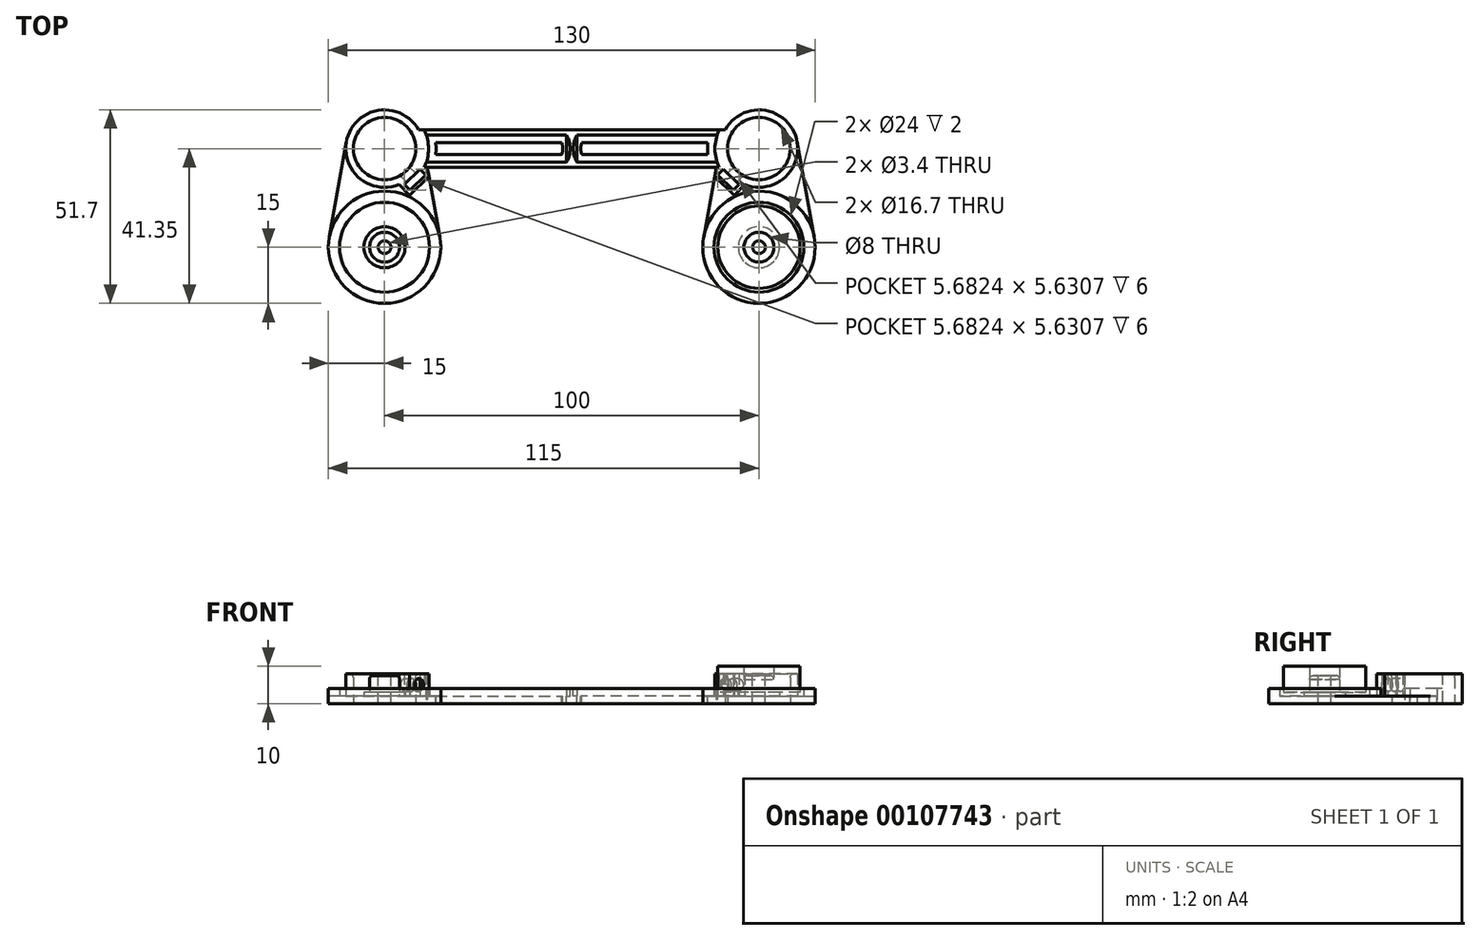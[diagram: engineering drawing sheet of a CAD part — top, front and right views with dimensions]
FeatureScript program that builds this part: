
annotation { "Feature Type Name" : "Feature", "Feature Type Description" : "" }
export const myFeature = defineFeature(function(context is Context, id is Id, definition is map)
    precondition{}
    {
        {
            assignVariable(context, id + "F0", {"name" : "BearingHeight", "anyValue" : 7});
        }
        {
            assignVariable(context, id + "F1", {"name" : "RodDistance", "anyValue" : 100});
        }
        {
            var Q0;
            Q0=qCreatedBy(makeId("Front.planeOp"),FACE);
            var sketch = newSketch(context, id + "F2", { "sketchPlane" : qUnion([Q0])});
            skLineSegment(sketch, "E0", {"start": v(0, 0) * mm, "end": v(0, 7.5) * mm});
            skLineSegment(sketch, "E1", {"start": v(0, 7.5) * mm, "end": v(4, 7.5) * mm});
            skLineSegment(sketch, "E2", {"start": v(4, 7.5) * mm, "end": v(4, 3) * mm});
            skLineSegment(sketch, "E3", {"start": v(4, 3) * mm, "end": v(5.5, 3) * mm});
            skLineSegment(sketch, "E4", {"start": v(5.5, 3) * mm, "end": v(5.5, 2) * mm});
            skLineSegment(sketch, "E5", {"start": v(5.5, 2) * mm, "end": v(11, 2) * mm});
            skLineSegment(sketch, "E6", {"start": v(11, 2) * mm, "end": v(12, 2) * mm});
            skLineSegment(sketch, "E7", {"start": v(12, 2) * mm, "end": v(12, 4) * mm});
            skLineSegment(sketch, "E8", {"start": v(12, 4) * mm, "end": v(15, 4) * mm});
            skLineSegment(sketch, "E9", {"start": v(15, 4) * mm, "end": v(15, 0) * mm});
            skLineSegment(sketch, "E10", {"start": v(15, 0) * mm, "end": v(0, 0) * mm});
            skSolve(sketch);
        }
        {
            var Q0;
            Q0=qSketchRegion(id+"F2",true);
            var Q1;
            Q1=sQuery(id+"F2.wireOp",EDGE,"E0");
            revolve(context, id + "F3", {"entities" : qUnion([Q0]), "axis" : qUnion([Q1]), "revolveType" : RevolveType.FULL});
        }
        {
            var Q0;
            Q0=makeQuery(id+"F3.opRevolve","SWEPT_FACE",FACE,{"disambiguationData":[OSD([sQuery(id+"F2.wireOp",EDGE,"E1")])]});
            var sketch = newSketch(context, id + "F4", { "sketchPlane" : qUnion([Q0])});
            skCircle(sketch, "E11", {"center": v(0, 0) * mm, "radius": 1.7 * mm});
            skSolve(sketch);
        }
        {
            var Q0;
            Q0=makeQuery(id+"F4.imprint","IMPRINT",FACE,{"disambiguationData":[TD([[makeQuery(id+"F4.imprint","IMPRINT",EDGE,{"derivedFrom":sQuery(id+"F4.wireOp",EDGE,"E11")}),1.0]])]});
            extrude(context, id + "F5", {"entities" : qUnion([Q0]), "operationType" : NewBodyOperationType.REMOVE, "endBound" : BoundingType.UP_TO_NEXT, "oppositeDirection" : true, "depth" : 25 * mm});
        }
        {
            var Q0;
            Q0=makeQuery(id+"F3.opRevolve","SWEPT_EDGE",EDGE,{"disambiguationData":[OSD([sQuery(id+"F2.wireOp",EDGE,"E1"),sQuery(id+"F2.wireOp",EDGE,"E2")])]});
            fillet(context, id + "F6", {"entities" : qUnion([Q0]), "radius" : 1 * mm, "tangentPropagation" : true, "allowEdgeOverflow" : false});
        }
        {
            var Q0;
            Q0=makeQuery(id+"F3.opRevolve","SWEPT_FACE",FACE,{"disambiguationData":[OSD([sQuery(id+"F2.wireOp",EDGE,"E10")])]});
            var sketch = newSketch(context, id + "F7", { "sketchPlane" : qUnion([Q0])});
            skCircle(sketch, "E12.0", {"center": v(0, 0) * mm, "radius": 15 * mm});
            skLineSegment(sketch, "E13", {"start": v(0, -26.35) * mm, "end": v(0, 0) * mm, "construction": true});
            skCircle(sketch, "E14", {"center": v(0, -26.35) * mm, "radius": 10.35 * mm});
            skLineSegment(sketch, "E15", {"start": v(-14.76, -2.65) * mm, "end": v(-10.19, -28.18) * mm});
            skLineSegment(sketch, "E16", {"start": v(14.76, -2.65) * mm, "end": v(10.19, -28.18) * mm});
            skCircle(sketch, "E17", {"center": v(0, -26.35) * mm, "radius": 8.35 * mm});
            skLineSegment(sketch, "E18", {"start": v(-3.82, -16.73) * mm, "end": v(-6.62, -13.88) * mm});
            skLineSegment(sketch, "E19", {"start": v(-6.62, -13.88) * mm, "end": v(-12.34, -19.47) * mm});
            skLineSegment(sketch, "E20", {"start": v(-12.34, -19.47) * mm, "end": v(-9.54, -22.33) * mm});
            skLineSegment(sketch, "E21", {"start": v(0, -26.35) * mm, "end": v(-9.48, -16.67) * mm, "construction": true});
            skLineSegment(sketch, "E22.bottom", {"start": v(-9.45, -20.85) * mm, "end": v(-5.3, -16.79) * mm});
            skLineSegment(sketch, "E22.top", {"start": v(-11, -19.28) * mm, "end": v(-6.85, -15.22) * mm});
            skLineSegment(sketch, "E22.left", {"start": v(-9.45, -20.85) * mm, "end": v(-11, -19.28) * mm});
            skLineSegment(sketch, "E22.right", {"start": v(-5.3, -16.79) * mm, "end": v(-6.85, -15.22) * mm});
            skPoint(sketch, "E22.middle", {"position": v(-8.15, -18.03) * mm});
            skLineSegment(sketch, "E23", {"start": v(-50, 9.03) * mm, "end": v(-50, -35.22) * mm, "construction": true});
            skLineSegment(sketch, "E24", {"start": v(0, -26.35) * mm, "end": v(-50, -26.35) * mm, "construction": true});
            skLineSegment(sketch, "E25", {"start": v(-9.06, -21.35) * mm, "end": v(-50, -21.35) * mm});
            skLineSegment(sketch, "E26.MirrorCS", {"start": v(-9.06, -31.35) * mm, "end": v(-50, -31.35) * mm});
            skLineSegment(sketch, "E27", {"start": v(-50, -31.35) * mm, "end": v(-50, -21.35) * mm});
            skSolve(sketch);
        }
        {
            var Q0;
            {var subQ0=sQuery(id+"F7.wireOp",EDGE,"E16");Q0=makeQuery(id+"F7.imprint","IMPRINT",FACE,{"disambiguationData":[TD([[makeQuery(id+"F7.imprint","IMPRINT",EDGE,{"derivedFrom":subQ0}),-1.0]])]});}
            var Q1;
            Q1=makeQuery(id+"F7.imprint","IMPRINT",FACE,{"disambiguationData":[TD([[makeQuery(id+"F7.imprint","IMPRINT",EDGE,{"derivedFrom":sQuery(id+"F7.wireOp",EDGE,"E17")}),-1.0]])]});
            var Q2;
            {var subQ0=sQuery(id+"F7.wireOp",EDGE,"E18");Q2=makeQuery(id+"F7.imprint","IMPRINT",FACE,{"disambiguationData":[TD([[makeQuery(id+"F7.imprint","IMPRINT",EDGE,{"derivedFrom":subQ0}),1.0]])]});}
            var Q3;
            {var subQ1=sQuery(id+"F7.wireOp",EDGE,"E22.bottom");Q3=makeQuery(id+"F7.imprint","IMPRINT",FACE,{"disambiguationData":[TD([[makeQuery(id+"F7.imprint","IMPRINT",EDGE,{"derivedFrom":subQ1}),1.0]])]});}
            var Q4;
            {var subQ0=sQuery(id+"F7.wireOp",EDGE,"E15");var subQ1=sQuery(id+"F7.wireOp",EDGE,"E14");var subQ2=makeQuery(id+"F7.imprint","INTERSECT",VERTEX,{"derivedFrom":[subQ1,subQ0]});Q4=makeQuery(id+"F7.imprint","IMPRINT",FACE,{"disambiguationData":[TD([[makeQuery(id+"F7.imprint","IMPRINT",EDGE,{"disambiguationData":[TD([[subQ2,1.0]])],"derivedFrom":subQ1}),-1.0]])]});}
            var Q5;
            Q5=makeQuery(id+"F7.imprint","IMPRINT",FACE,{"disambiguationData":[TD([[makeQuery(id+"F7.imprint","IMPRINT",EDGE,{"derivedFrom":makeQuery(id+"F5.boolean.opBoolean","COPY",EDGE,{"derivedFrom":makeQuery(id+"F5.opExtrude","TWEAK_EDGE",EDGE,{"derivedFrom":[makeQuery(id+"F3.opRevolve","SWEPT_FACE",FACE,{"disambiguationData":[OSD([sQuery(id+"F2.wireOp",EDGE,"E10")])]}),makeQuery(id+"F4.imprint","IMPRINT",EDGE,{"derivedFrom":sQuery(id+"F4.wireOp",EDGE,"E11")})]})})}),-1.0]])]});
            var Q6;
            Q6=makeQuery(id+"F3.opRevolve","SWEPT_FACE",FACE,{"disambiguationData":[OSD([sQuery(id+"F2.wireOp",EDGE,"E10")])]});
            var Q7;
            Q7=makeQuery(id+"F7.imprint","IMPRINT",FACE,{"disambiguationData":[TD([[makeQuery(id+"F7.imprint","IMPRINT",EDGE,{"derivedFrom":sQuery(id+"F7.wireOp",EDGE,"bac2def9-7b5b-4e3d-a74a-6b2987ab829d0.MirrorCS")}),1.0]])]});
            var Q8;
            Q8=makeQuery(id+"F7.imprint","IMPRINT",FACE,{"disambiguationData":[TD([[makeQuery(id+"F7.imprint","IMPRINT",EDGE,{"derivedFrom":sQuery(id+"F7.wireOp",EDGE,"bac2def9-7b5b-4e3d-a74a-6b2987ab829d0.MirrorCS")}),-1.0]])]});
            var Q9;
            {var subQ10=sQuery(id+"F7.wireOp",EDGE,"E18");Q9=makeQuery(id+"F7.imprint","IMPRINT",FACE,{"disambiguationData":[TD([[makeQuery(id+"F7.imprint","IMPRINT",EDGE,{"derivedFrom":subQ10}),-1.0]])]});}
            var Q10;
            {var subQ0=sQuery(id+"F7.wireOp",EDGE,"E26.MirrorCS");Q10=makeQuery(id+"F7.imprint","IMPRINT",FACE,{"disambiguationData":[TD([[makeQuery(id+"F7.imprint","IMPRINT",EDGE,{"derivedFrom":subQ0}),-1.0]])]});}
            var Q11;
            {var subQ0=sQuery(id+"F7.wireOp",EDGE,"E20");var subQ1=sQuery(id+"F7.wireOp",EDGE,"E14");var subQ2=makeQuery(id+"F7.imprint","INTERSECT",VERTEX,{"derivedFrom":[subQ1,subQ0]});Q11=makeQuery(id+"F7.imprint","IMPRINT",FACE,{"disambiguationData":[TD([[makeQuery(id+"F7.imprint","IMPRINT",EDGE,{"disambiguationData":[TD([[subQ2,1.0]])],"derivedFrom":subQ1}),-1.0]])]});}
            var Q12;
            Q12=makeQuery(id+"F7.imprint","IMPRINT",FACE,{"disambiguationData":[TD([[makeQuery(id+"F7.imprint","IMPRINT",EDGE,{"derivedFrom":sQuery(id+"F7.wireOp",EDGE,"5ed84967-02fd-4a5b-a8fa-f03f07f36d90")}),1.0]])]});
            var Q13;
            Q13=makeQuery(id+"F3.opRevolve","SWEPT_FACE",FACE,{"disambiguationData":[OSD([sQuery(id+"F2.wireOp",EDGE,"E5"),sQuery(id+"F2.wireOp",EDGE,"E6")])]});
            extrude(context, id + "F8", {"entities" : qUnion([Q0, Q1, Q2, Q3, Q4, Q5, Q6, Q7, Q8, Q9, Q10, Q11, Q12]), "operationType" : NewBodyOperationType.ADD, "endBound" : BoundingType.UP_TO_SURFACE, "oppositeDirection" : true, "endBoundEntityFace" : qUnion([Q13]), "depth" : 25 * mm});
        }
        {
            var Q0;
            Q0=makeQuery(id+"F7.imprint","IMPRINT",FACE,{"disambiguationData":[TD([[makeQuery(id+"F7.imprint","IMPRINT",EDGE,{"derivedFrom":sQuery(id+"F7.wireOp",EDGE,"E17")}),-1.0]])]});
            var Q1;
            {var subQ0=sQuery(id+"F7.wireOp",EDGE,"E18");Q1=makeQuery(id+"F7.imprint","IMPRINT",FACE,{"disambiguationData":[TD([[makeQuery(id+"F7.imprint","IMPRINT",EDGE,{"derivedFrom":subQ0}),1.0]])]});}
            var Q2;
            Q2=makeQuery(id+"F7.imprint","IMPRINT",FACE,{"disambiguationData":[TD([[makeQuery(id+"F7.imprint","IMPRINT",EDGE,{"derivedFrom":sQuery(id+"F7.wireOp",EDGE,"bac2def9-7b5b-4e3d-a74a-6b2987ab829d0.MirrorCS")}),1.0]])]});
            extrude(context, id + "F9", {"entities" : qUnion([Q0, Q1, Q2]), "operationType" : NewBodyOperationType.ADD, "oppositeDirection" : true, "depth" : 8 * mm});
        }
        {
            var Q0;
            Q0=makeQuery(id+"F9.opExtrude","SWEPT_FACE",FACE,{"disambiguationData":[OSD([sQuery(id+"F7.wireOp",EDGE,"E19")])]});
            var sketch = newSketch(context, id + "F10", { "sketchPlane" : qUnion([Q0])});
            skLineSegment(sketch, "E28", {"start": v(-14.44, 5) * mm, "end": v(-21.74, 5) * mm, "construction": true});
            skPoint(sketch, "E29", {"position": v(-18.1, 5) * mm});
            skCircle(sketch, "E30", {"center": v(-18.1, 5) * mm, "radius": 1.7 * mm});
            skSolve(sketch);
        }
        {
            var Q0;
            Q0=makeQuery(id+"F10.imprint","IMPRINT",FACE,{"disambiguationData":[TD([[makeQuery(id+"F10.imprint","IMPRINT",EDGE,{"derivedFrom":sQuery(id+"F10.wireOp",EDGE,"E30")}),1.0]])]});
            var Q1;
            {var subQ0=sQuery(id+"F7.wireOp",EDGE,"E17");Q1=makeQuery(id+"F9.boolean.opBoolean","MERGE",FACE,{"derivedFrom":[makeQuery(id+"F8.opExtrude","SWEPT_FACE",FACE,{"disambiguationData":[OSD([subQ0])]}),makeQuery(id+"F9.opExtrude","SWEPT_FACE",FACE,{"disambiguationData":[OSD([subQ0])]})]});}
            extrude(context, id + "F11", {"entities" : qUnion([Q0]), "operationType" : NewBodyOperationType.REMOVE, "endBound" : BoundingType.UP_TO_SURFACE, "oppositeDirection" : true, "endBoundEntityFace" : qUnion([Q1]), "depth" : 25 * mm});
        }
        {
            var Q0;
            Q0=makeQuery(id+"F3.opRevolve","SWEPT_FACE",FACE,{"disambiguationData":[OSD([sQuery(id+"F2.wireOp",EDGE,"E3")])]});
            var sketch = newSketch(context, id + "F12", { "sketchPlane" : qUnion([Q0])});
            skCircle(sketch, "E31.0", {"center": v(0, 0) * mm, "radius": 4 * mm});
            skCircle(sketch, "E32", {"center": v(0, 0) * mm, "radius": 11 * mm});
            skSolve(sketch);
        }
        {
            var Q0;
            Q0=qSketchRegion(id+"F12",true);
            extrude(context, id + "F13", {"entities" : qUnion([Q0]), "depth" : (getVariable(context, 'BearingHeight')) * mm});
        }
        {
            var Q0;
            Q0=makeQuery(id+"F9.opExtrude","CAP_EDGE",EDGE,{"disambiguationData":[OSD([sQuery(id+"F7.wireOp",EDGE,"E17")])],"isStart":false});
            fillet(context, id + "F14", {"entities" : qUnion([Q0]), "radius" : 1 * mm, "tangentPropagation" : true, "allowEdgeOverflow" : false});
        }
        {
            var Q0;
            {var subQ0=sQuery(id+"F7.wireOp",EDGE,"E26.MirrorCS");var subQ1=sQuery(id+"F7.wireOp",EDGE,"E25");var subQ2=sQuery(id+"F7.wireOp",EDGE,"E20");var subQ3=sQuery(id+"F7.wireOp",EDGE,"E16");var subQ4=sQuery(id+"F7.wireOp",EDGE,"E14");var subQ7=sQuery(id+"F7.wireOp",EDGE,"E15");var subQ10=sQuery(id+"F7.wireOp",EDGE,"E27");var subQ11=sQuery(id+"F2.wireOp",EDGE,"E10");Q0=makeQuery(id+"F9.boolean.opBoolean","SPLIT",FACE,{"disambiguationData":[TD([makeQuery(id+"F8.opExtrude","SWEPT_FACE",FACE,{"disambiguationData":[OSD([subQ2])]})])],"derivedFrom":makeQuery(id+"F8.boolean.opBoolean","MERGE",FACE,{"derivedFrom":[makeQuery(id+"F8.opExtrude","CAP_FACE",FACE,{"disambiguationData":[OSD([subQ11])],"isStart":false}),makeQuery(id+"F8.opExtrude","CAP_FACE",FACE,{"disambiguationData":[OSD([subQ11,sQuery(id+"F4.wireOp",EDGE,"E11"),sQuery(id+"F7.wireOp",EDGE,"E12.0"),subQ4,subQ7,subQ3,sQuery(id+"F7.wireOp",EDGE,"E17"),subQ2,subQ1,subQ0,subQ10])],"isStart":false})]})});}
            var sketch = newSketch(context, id + "F15", { "sketchPlane" : qUnion([Q0])});
            skLineSegment(sketch, "E33.0", {"start": v(-48.6, 22.75) * mm, "end": v(-11.18, 22.75) * mm});
            skLineSegment(sketch, "E33.1", {"start": v(-48.6, 22.75) * mm, "end": v(-48.6, 29.95) * mm});
            skLineSegment(sketch, "E33.2", {"start": v(-48.6, 29.95) * mm, "end": v(-11.18, 29.95) * mm});
            skArc(sketch, "E33.3", {"start": v(-11.18, 22.75) * mm, "mid": v(-11.75, 26.35) * mm, "end": v(-11.18, 29.95) * mm});
            skSolve(sketch);
        }
        {
            var Q0;
            Q0=makeQuery(id+"F15.imprint","IMPRINT",FACE,{"disambiguationData":[TD([[makeQuery(id+"F15.imprint","IMPRINT",EDGE,{"derivedFrom":sQuery(id+"F15.wireOp",EDGE,"E33.0")}),-1.0]])]});
            extrude(context, id + "F16", {"entities" : qUnion([Q0]), "operationType" : NewBodyOperationType.ADD, "depth" : 2 * mm});
        }
        {
            var Q0;
            {var subQ0=makeQuery(id+"F16.opExtrude","CAP_FACE",FACE,{"disambiguationData":[OSD([sQuery(id+"F2.wireOp",EDGE,"E10"),sQuery(id+"F4.wireOp",EDGE,"E11"),sQuery(id+"F7.wireOp",EDGE,"E12.0"),sQuery(id+"F7.wireOp",EDGE,"E14"),sQuery(id+"F7.wireOp",EDGE,"E15"),sQuery(id+"F7.wireOp",EDGE,"E16"),sQuery(id+"F7.wireOp",EDGE,"E17"),sQuery(id+"F7.wireOp",EDGE,"E20"),sQuery(id+"F7.wireOp",EDGE,"E25"),sQuery(id+"F7.wireOp",EDGE,"E26.MirrorCS"),sQuery(id+"F7.wireOp",EDGE,"E27"),sQuery(id+"F15.wireOp",EDGE,"E33.0"),sQuery(id+"F15.wireOp",EDGE,"E33.1"),sQuery(id+"F15.wireOp",EDGE,"E33.2"),sQuery(id+"F15.wireOp",EDGE,"E33.3")])],"isStart":false});Q0=makeQuery(id+"F25.boolean.opBoolean","MERGE",FACE,{"derivedFrom":[subQ0,makeQuery(id+"F25.opPattern","COPY",FACE,{"derivedFrom":subQ0,"instanceName":"1"})]});}
            var sketch = newSketch(context, id + "F17", { "sketchPlane" : qUnion([Q0])});
            skArc(sketch, "E34.0", {"start": v(-10.29, 20.67) * mm, "mid": v(-11.75, 26.35) * mm, "end": v(-10.29, 32.03) * mm});
            skLineSegment(sketch, "E35", {"start": v(-9.06, 31.35) * mm, "end": v(-10.63, 31.35) * mm});
            skLineSegment(sketch, "E36", {"start": v(-9.06, 21.35) * mm, "end": v(-10.63, 21.35) * mm});
            skArc(sketch, "E37", {"start": v(-48.6, 29.95) * mm, "mid": v(-49.6, 26.35) * mm, "end": v(-48.6, 22.75) * mm});
            skSolve(sketch);
        }
        {
            var Q0;
            Q0=qSketchRegion(id+"F17",true);
            var Q1;
            Q1=makeQuery(id+"F17.imprint","IMPRINT",FACE,{"disambiguationData":[TD([[makeQuery(id+"F17.imprint","IMPRINT",EDGE,{"derivedFrom":sQuery(id+"F17.wireOp",EDGE,"E37")}),1.0]])]});
            var Q2;
            {var subQ0=sQuery(id+"F7.wireOp",EDGE,"E26.MirrorCS");var subQ1=sQuery(id+"F7.wireOp",EDGE,"E25");var subQ2=sQuery(id+"F7.wireOp",EDGE,"E20");var subQ3=sQuery(id+"F7.wireOp",EDGE,"E16");var subQ4=sQuery(id+"F7.wireOp",EDGE,"E14");var subQ7=sQuery(id+"F7.wireOp",EDGE,"E15");var subQ10=sQuery(id+"F7.wireOp",EDGE,"E27");var subQ11=sQuery(id+"F2.wireOp",EDGE,"E10");Q2=makeQuery(id+"F9.boolean.opBoolean","SPLIT",FACE,{"disambiguationData":[TD([makeQuery(id+"F8.opExtrude","SWEPT_FACE",FACE,{"disambiguationData":[OSD([subQ2])]})])],"derivedFrom":makeQuery(id+"F8.boolean.opBoolean","MERGE",FACE,{"derivedFrom":[makeQuery(id+"F8.opExtrude","CAP_FACE",FACE,{"disambiguationData":[OSD([subQ11])],"isStart":false}),makeQuery(id+"F8.opExtrude","CAP_FACE",FACE,{"disambiguationData":[OSD([subQ11,sQuery(id+"F4.wireOp",EDGE,"E11"),sQuery(id+"F7.wireOp",EDGE,"E12.0"),subQ4,subQ7,subQ3,sQuery(id+"F7.wireOp",EDGE,"E17"),subQ2,subQ1,subQ0,subQ10])],"isStart":false})]})});}
            extrude(context, id + "F18", {"entities" : qUnion([Q0, Q1]), "operationType" : NewBodyOperationType.REMOVE, "endBound" : BoundingType.UP_TO_SURFACE, "oppositeDirection" : true, "endBoundEntityFace" : qUnion([Q2]), "depth" : 25 * mm});
        }
        {
            var Q0;
            {var subQ1=makeQuery(id+"F16.opExtrude","CAP_EDGE",EDGE,{"disambiguationData":[OSD([sQuery(id+"F15.wireOp",EDGE,"E33.0")])],"isStart":false});Q0=makeQuery(id+"F17.imprint","IMPRINT",FACE,{"disambiguationData":[TD([[makeQuery(id+"F17.imprint","IMPRINT",EDGE,{"derivedFrom":subQ1}),1.0]])]});}
            var sketch = newSketch(context, id + "F19", { "sketchPlane" : qUnion([Q0])});
            skArc(sketch, "E38.0", {"start": v(-13.66, 24.75) * mm, "mid": v(-13.75, 26.35) * mm, "end": v(-13.66, 27.95) * mm});
            skLineSegment(sketch, "E38.1", {"start": v(-47.34, 24.75) * mm, "end": v(-13.66, 24.75) * mm});
            skArc(sketch, "E38.2", {"start": v(-47.34, 27.95) * mm, "mid": v(-47.6, 26.35) * mm, "end": v(-47.34, 24.75) * mm});
            skLineSegment(sketch, "E38.3", {"start": v(-47.34, 27.95) * mm, "end": v(-13.66, 27.95) * mm});
            skSolve(sketch);
        }
        {
            var Q0;
            Q0=makeQuery(id+"F19.imprint","IMPRINT",FACE,{"disambiguationData":[TD([[makeQuery(id+"F19.imprint","IMPRINT",EDGE,{"derivedFrom":sQuery(id+"F19.wireOp",EDGE,"E38.0")}),1.0]])]});
            extrude(context, id + "F20", {"entities" : qUnion([Q0]), "operationType" : NewBodyOperationType.REMOVE, "oppositeDirection" : true, "depth" : 25 * mm});
        }
        {
            var Q0;
            {var subQ0=sQuery(id+"F7.wireOp",EDGE,"E20");var subQ1=sQuery(id+"F7.wireOp",EDGE,"E15");var subQ2=makeQuery(id+"F7.imprint","INTERSECT",VERTEX,{"derivedFrom":[subQ1,subQ0]});Q0=makeQuery(id+"F7.imprint","IMPRINT",FACE,{"disambiguationData":[TD([[makeQuery(id+"F7.imprint","IMPRINT",EDGE,{"disambiguationData":[TD([[subQ2,-1.0]])],"derivedFrom":subQ1}),1.0]])]});}
            var Q1;
            {var subQ0=makeQuery(id+"F16.opExtrude","CAP_FACE",FACE,{"disambiguationData":[OSD([sQuery(id+"F2.wireOp",EDGE,"E10"),sQuery(id+"F4.wireOp",EDGE,"E11"),sQuery(id+"F7.wireOp",EDGE,"E12.0"),sQuery(id+"F7.wireOp",EDGE,"E14"),sQuery(id+"F7.wireOp",EDGE,"E15"),sQuery(id+"F7.wireOp",EDGE,"E16"),sQuery(id+"F7.wireOp",EDGE,"E17"),sQuery(id+"F7.wireOp",EDGE,"E20"),sQuery(id+"F7.wireOp",EDGE,"E25"),sQuery(id+"F7.wireOp",EDGE,"E26.MirrorCS"),sQuery(id+"F7.wireOp",EDGE,"E27"),sQuery(id+"F15.wireOp",EDGE,"E33.0"),sQuery(id+"F15.wireOp",EDGE,"E33.1"),sQuery(id+"F15.wireOp",EDGE,"E33.2"),sQuery(id+"F15.wireOp",EDGE,"E33.3")])],"isStart":false});Q1=makeQuery(id+"F25.boolean.opBoolean","MERGE",FACE,{"derivedFrom":[subQ0,makeQuery(id+"F25.opPattern","COPY",FACE,{"derivedFrom":subQ0,"instanceName":"1"})]});}
            extrude(context, id + "F21", {"entities" : qUnion([Q0]), "operationType" : NewBodyOperationType.ADD, "endBound" : BoundingType.UP_TO_SURFACE, "oppositeDirection" : true, "endBoundEntityFace" : qUnion([Q1]), "depth" : 25 * mm});
        }
        {
            var Q0;
            {var subQ0=sQuery(id+"F17.wireOp",EDGE,"E35");Q0=makeQuery(id+"F17.imprint","IMPRINT",FACE,{"disambiguationData":[TD([[makeQuery(id+"F17.imprint","IMPRINT",EDGE,{"derivedFrom":subQ0}),-1.0]])]});}
            var sketch = newSketch(context, id + "F22", { "sketchPlane" : qUnion([Q0])});
            skArc(sketch, "E39.0.0", {"start": v(-11.18, 22.75) * mm, "mid": v(-10.93, 22.04) * mm, "end": v(-10.63, 21.35) * mm});
            skLineSegment(sketch, "E39.0.1", {"start": v(-10.63, 21.35) * mm, "end": v(-10.5, 21.35) * mm});
            skLineSegment(sketch, "E39.0.2", {"start": v(-10.5, 21.35) * mm, "end": v(-9.06, 21.35) * mm});
            skArc(sketch, "E39.0.3", {"start": v(-9.06, 21.35) * mm, "mid": v(-10.35, 26.35) * mm, "end": v(-9.06, 31.35) * mm});
            skLineSegment(sketch, "E39.0.4", {"start": v(-9.06, 31.35) * mm, "end": v(-10.63, 31.35) * mm});
            skArc(sketch, "E39.0.5", {"start": v(-10.63, 31.35) * mm, "mid": v(-10.93, 30.66) * mm, "end": v(-11.18, 29.95) * mm});
            skArc(sketch, "E39.0.6", {"start": v(-11.18, 29.95) * mm, "mid": v(-11.75, 26.35) * mm, "end": v(-11.18, 22.75) * mm});
            skLineSegment(sketch, "E39.1", {"start": v(-9.06, 21.35) * mm, "end": v(-50, 21.35) * mm});
            skLineSegment(sketch, "E39.2", {"start": v(-14.76, 2.65) * mm, "end": v(-10.19, 28.18) * mm});
            skLineSegment(sketch, "E39.3", {"start": v(-12.34, 19.47) * mm, "end": v(-9.54, 22.33) * mm});
            skSolve(sketch);
        }
        {
            var Q0;
            {var subQ3=sQuery(id+"F22.wireOp",EDGE,"E39.0.0");var subQ7=sQuery(id+"F22.wireOp",EDGE,"E39.1");var subQ9=makeQuery(id+"F22.imprint","INTERSECT",VERTEX,{"derivedFrom":[subQ3,subQ7]});Q0=makeQuery(id+"F22.imprint","IMPRINT",FACE,{"disambiguationData":[TD([[makeQuery(id+"F22.imprint","IMPRINT",EDGE,{"disambiguationData":[TD([[subQ9,-1.0]])],"derivedFrom":subQ3}),-1.0]])]});}
            var Q1;
            {var subQ0=sQuery(id+"F22.wireOp",EDGE,"E39.1");var subQ1=sQuery(id+"F22.wireOp",EDGE,"E39.0.0");var subQ2=makeQuery(id+"F22.imprint","INTERSECT",VERTEX,{"derivedFrom":[subQ1,subQ0]});Q1=makeQuery(id+"F22.imprint","IMPRINT",FACE,{"disambiguationData":[TD([[makeQuery(id+"F22.imprint","IMPRINT",EDGE,{"disambiguationData":[TD([[subQ2,-1.0]])],"derivedFrom":subQ1}),1.0]])]});}
            var Q2;
            {var subQ0=sQuery(id+"F22.wireOp",EDGE,"E39.1");var subQ1=makeQuery(id+"F22.imprint","INTERSECT",VERTEX,{"derivedFrom":[sQuery(id+"F22.wireOp",EDGE,"E39.0.0"),subQ0]});Q2=makeQuery(id+"F22.imprint","IMPRINT",FACE,{"disambiguationData":[TD([[makeQuery(id+"F22.imprint","IMPRINT",EDGE,{"disambiguationData":[TD([[subQ1,-1.0]])],"derivedFrom":subQ0}),1.0]])]});}
            var Q3;
            {var subQ0=sQuery(id+"F22.wireOp",EDGE,"E39.1");var subQ1=sQuery(id+"F22.wireOp",EDGE,"E39.0.3");var subQ2=makeQuery(id+"F22.imprint","INTERSECT",VERTEX,{"derivedFrom":[subQ1,subQ0]});Q3=makeQuery(id+"F22.imprint","IMPRINT",FACE,{"disambiguationData":[TD([[makeQuery(id+"F22.imprint","IMPRINT",EDGE,{"disambiguationData":[TD([[subQ2,-1.0]])],"derivedFrom":subQ1}),1.0]])]});}
            var Q4;
            {var subQ0=sQuery(id+"F17.wireOp",EDGE,"E35");Q4=makeQuery(id+"F17.imprint","IMPRINT",FACE,{"disambiguationData":[TD([[makeQuery(id+"F17.imprint","IMPRINT",EDGE,{"derivedFrom":subQ0}),-1.0]])]});}
            var Q5;
            Q5=makeQuery(id+"F9.opExtrude","CAP_FACE",FACE,{"disambiguationData":[OSD([sQuery(id+"F7.wireOp",EDGE,"E14"),sQuery(id+"F7.wireOp",EDGE,"E15"),sQuery(id+"F7.wireOp",EDGE,"E17"),sQuery(id+"F7.wireOp",EDGE,"E18"),sQuery(id+"F7.wireOp",EDGE,"E19"),sQuery(id+"F7.wireOp",EDGE,"E20"),sQuery(id+"F7.wireOp",EDGE,"E22.bottom"),sQuery(id+"F7.wireOp",EDGE,"E22.top"),sQuery(id+"F7.wireOp",EDGE,"E22.left"),sQuery(id+"F7.wireOp",EDGE,"E22.right"),sQuery(id+"F7.wireOp",EDGE,"E25")])],"isStart":false});
            extrude(context, id + "F23", {"entities" : qUnion([Q0, Q1, Q2, Q3, Q4]), "operationType" : NewBodyOperationType.ADD, "endBound" : BoundingType.UP_TO_SURFACE, "endBoundEntityFace" : qUnion([Q5]), "depth" : 25 * mm});
        }
        {
            var Q0;
            Q0=qCreatedBy(makeId("Right.planeOp"),FACE);
            cPlane(context, id + "F24", {"entities" : qUnion([Q0]), "cplaneType" : CPlaneType.OFFSET, "offset" : (getVariable(context, 'RodDistance') / 2) * mm, "oppositeDirection" : true, "width" : 150 * mm, "height" : 150 * mm});
        }
        {
            var Q0;
            Q0=makeQuery(id+"F3.opRevolve","SWEPT_BODY",BODY,{"disambiguationData":[OSD([sQuery(id+"F2.wireOp",EDGE,"E0"),sQuery(id+"F2.wireOp",EDGE,"E1"),sQuery(id+"F2.wireOp",EDGE,"E2"),sQuery(id+"F2.wireOp",EDGE,"E3"),sQuery(id+"F2.wireOp",EDGE,"E4"),sQuery(id+"F2.wireOp",EDGE,"E5"),sQuery(id+"F2.wireOp",EDGE,"E6"),sQuery(id+"F2.wireOp",EDGE,"E7"),sQuery(id+"F2.wireOp",EDGE,"E8"),sQuery(id+"F2.wireOp",EDGE,"E9"),sQuery(id+"F2.wireOp",EDGE,"E10")])]});
            var Q1;
            Q1=qCreatedBy(id+"F24.planeOp",FACE);
            mirror(context, id + "F25", {"operationType" : NewBodyOperationType.ADD, "entities" : qUnion([Q0]), "mirrorPlane" : qUnion([Q1])});
        }
    });
